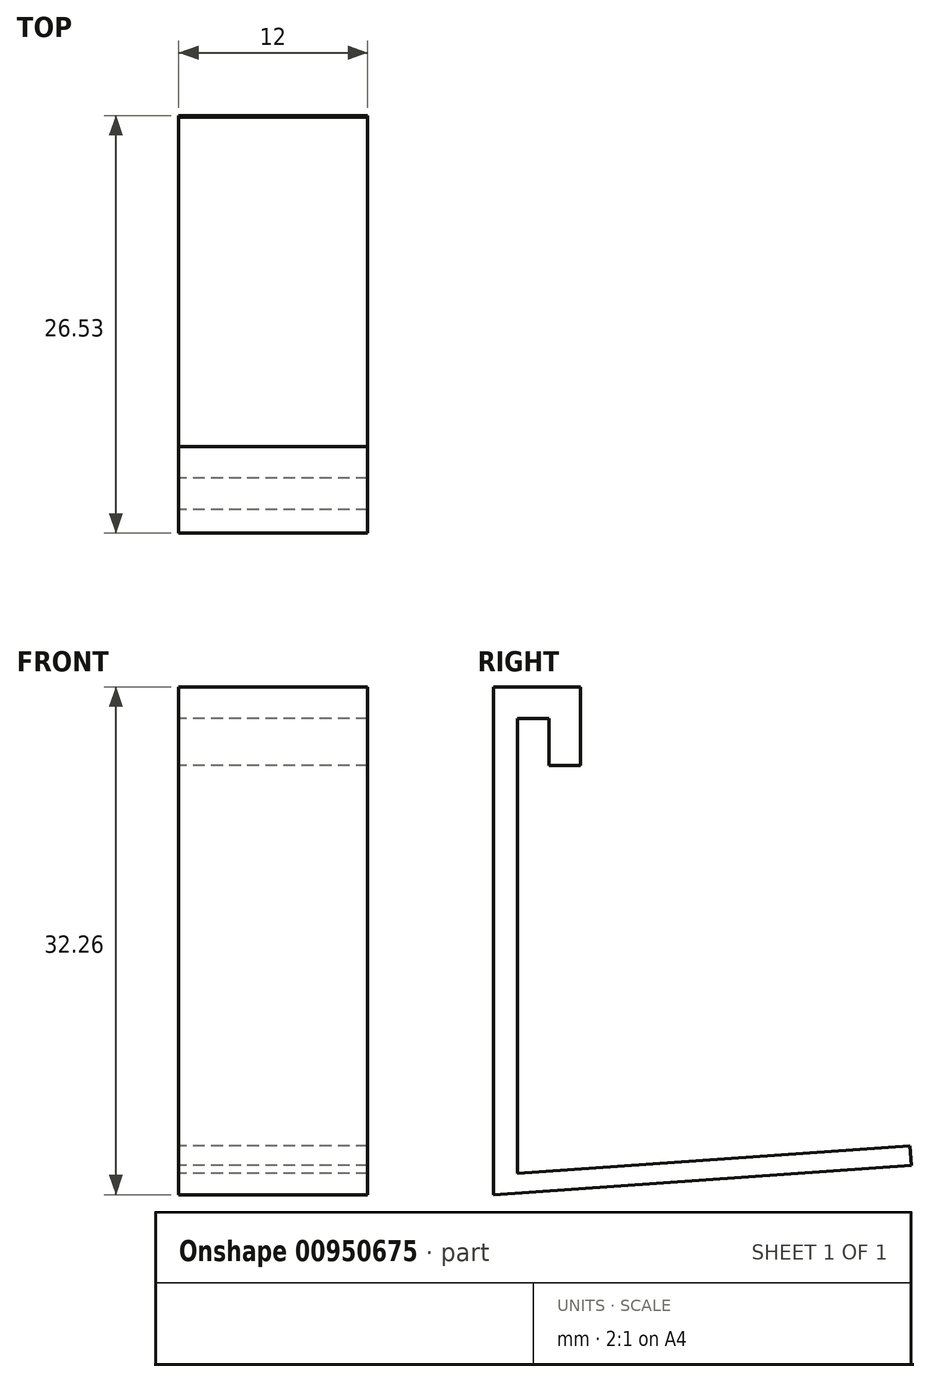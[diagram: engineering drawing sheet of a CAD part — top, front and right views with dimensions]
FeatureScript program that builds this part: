
annotation { "Feature Type Name" : "Feature", "Feature Type Description" : "" }
export const myFeature = defineFeature(function(context is Context, id is Id, definition is map)
    precondition{}
    {
        {
            var Q0;
            Q0=qCreatedBy(makeId("Front.planeOp"),FACE);
            var sketch = newSketch(context, id + "F0", { "sketchPlane" : qUnion([Q0])});
            skLineSegment(sketch, "E0.bottom", {"start": v(-42.47, 42.4) * mm, "end": v(-54.47, 42.4) * mm});
            skLineSegment(sketch, "E0.top", {"start": v(-42.47, 16.5) * mm, "end": v(-54.47, 16.5) * mm});
            skLineSegment(sketch, "E0.left", {"start": v(-42.47, 42.4) * mm, "end": v(-42.47, 16.5) * mm});
            skLineSegment(sketch, "E0.right", {"start": v(-54.47, 42.4) * mm, "end": v(-54.47, 16.5) * mm});
            skSolve(sketch);
        }
        {
            var Q0;
            Q0=makeQuery(id+"F0.imprint","IMPRINT",FACE,{"disambiguationData":[TD([[makeQuery(id+"F0.imprint","IMPRINT",EDGE,{"derivedFrom":sQuery(id+"F0.wireOp",EDGE,"E0.bottom")}),1.0]])]});
            extrude(context, id + "F1", {"entities" : qUnion([Q0]), "depth" : 1.5 * mm, "offsetDistance" : 25 * mm});
        }
        {
            var Q0;
            Q0=makeQuery(id+"F1.opExtrude","CAP_FACE",FACE,{"disambiguationData":[OSD([sQuery(id+"F0.wireOp",EDGE,"E0.bottom"),sQuery(id+"F0.wireOp",EDGE,"E0.top"),sQuery(id+"F0.wireOp",EDGE,"E0.left"),sQuery(id+"F0.wireOp",EDGE,"E0.right")])],"isStart":false});
            var sketch = newSketch(context, id + "F2", { "sketchPlane" : qUnion([Q0])});
            skLineSegment(sketch, "E1.0", {"start": v(-42.47, 16.5) * mm, "end": v(-54.47, 16.5) * mm});
            skLineSegment(sketch, "E2", {"start": v(-54.47, 16.5) * mm, "end": v(-54.47, 15.26) * mm});
            skLineSegment(sketch, "E3", {"start": v(-54.47, 15.26) * mm, "end": v(-42.47, 15.26) * mm});
            skLineSegment(sketch, "E4", {"start": v(-42.47, 15.26) * mm, "end": v(-42.47, 16.5) * mm});
            skSolve(sketch);
        }
        {
            var Q0;
            Q0=makeQuery(id+"FgG7fGiDoCPkPZg_1.boolean.opBoolean","MERGE",FACE,{"derivedFrom":[makeQuery(id+"F1.opExtrude","SWEPT_FACE",FACE,{"disambiguationData":[OSD([sQuery(id+"F0.wireOp",EDGE,"E0.right")])]}),makeQuery(id+"FgG7fGiDoCPkPZg_1.opExtrude","SWEPT_FACE",FACE,{"disambiguationData":[OSD([sQuery(id+"F2.wireOp",EDGE,"E2")])]})]});
            var sketch = newSketch(context, id + "F3", { "sketchPlane" : qUnion([Q0])});
            skLineSegment(sketch, "E5.0", {"start": v(1.5, 42.4) * mm, "end": v(1.5, 15.26) * mm});
            skLineSegment(sketch, "E5.1", {"start": v(0, 42.4) * mm, "end": v(0, 16.5) * mm});
            skLineSegment(sketch, "E5.2", {"start": v(1.5, 42.4) * mm, "end": v(0, 42.4) * mm});
            skLineSegment(sketch, "E6", {"start": v(-2, 42.4) * mm, "end": v(-4, 42.4) * mm});
            skLineSegment(sketch, "E7", {"start": v(-4, 42.4) * mm, "end": v(-4, 45.4) * mm});
            skLineSegment(sketch, "E8", {"start": v(1.5, 45.4) * mm, "end": v(1.5, 42.4) * mm});
            skLineSegment(sketch, "E9", {"start": v(-2, 42.4) * mm, "end": v(-2, 45.4) * mm});
            skLineSegment(sketch, "E10", {"start": v(-4, 45.4) * mm, "end": v(-4, 47.4) * mm});
            skLineSegment(sketch, "E11", {"start": v(1.5, 47.4) * mm, "end": v(1.5, 45.4) * mm});
            skLineSegment(sketch, "E12", {"start": v(0, 45.4) * mm, "end": v(0, 42.4) * mm});
            skLineSegment(sketch, "E13", {"start": v(0, 45.4) * mm, "end": v(-2, 45.4) * mm});
            skLineSegment(sketch, "E14", {"start": v(-4, 47.4) * mm, "end": v(1.5, 47.4) * mm});
            skSolve(sketch);
        }
        {
            var Q0;
            Q0=makeQuery(id+"F3.imprint","IMPRINT",FACE,{"disambiguationData":[TD([[makeQuery(id+"F3.imprint","IMPRINT",EDGE,{"derivedFrom":sQuery(id+"F3.wireOp",EDGE,"E5.2")}),-1.0]])]});
            var Q1;
            Q1=makeQuery(id+"FgG7fGiDoCPkPZg_1.boolean.opBoolean","MERGE",FACE,{"derivedFrom":[makeQuery(id+"F1.opExtrude","SWEPT_FACE",FACE,{"disambiguationData":[OSD([sQuery(id+"F0.wireOp",EDGE,"E0.left")])]}),makeQuery(id+"FgG7fGiDoCPkPZg_1.opExtrude","SWEPT_FACE",FACE,{"disambiguationData":[OSD([sQuery(id+"F2.wireOp",EDGE,"E4")])]})]});
            extrude(context, id + "F4", {"entities" : qUnion([Q0]), "operationType" : NewBodyOperationType.ADD, "endBound" : BoundingType.UP_TO_SURFACE, "oppositeDirection" : true, "depth" : 25 * mm, "endBoundEntityFace" : qUnion([Q1]), "offsetDistance" : 25 * mm});
        }
        {
            var Q0;
            Q0=makeQuery(id+"F4.boolean.opBoolean","MERGE",FACE,{"derivedFrom":[makeQuery(id+"F1.opExtrude","SWEPT_FACE",FACE,{"disambiguationData":[OSD([sQuery(id+"F0.wireOp",EDGE,"E0.right")])]}),makeQuery(id+"F4.opExtrude","CAP_FACE",FACE,{"disambiguationData":[OSD([sQuery(id+"F3.wireOp",EDGE,"E5.2"),sQuery(id+"F3.wireOp",EDGE,"E6"),sQuery(id+"F3.wireOp",EDGE,"E7"),sQuery(id+"F3.wireOp",EDGE,"E8"),sQuery(id+"F3.wireOp",EDGE,"E9"),sQuery(id+"F3.wireOp",EDGE,"E10"),sQuery(id+"F3.wireOp",EDGE,"E11"),sQuery(id+"F3.wireOp",EDGE,"E12"),sQuery(id+"F3.wireOp",EDGE,"E13"),sQuery(id+"F3.wireOp",EDGE,"E14")])],"isStart":true})]});
            var sketch = newSketch(context, id + "F5", { "sketchPlane" : qUnion([Q0])});
            skLineSegment(sketch, "E15", {"start": v(0, 16.5) * mm, "end": v(-24.94, 18.25) * mm});
            skLineSegment(sketch, "E16", {"start": v(-24.94, 18.25) * mm, "end": v(-25.03, 17) * mm});
            skLineSegment(sketch, "E17", {"start": v(-25.03, 17) * mm, "end": v(1.5, 15.15) * mm});
            skLineSegment(sketch, "E18", {"start": v(1.5, 15.15) * mm, "end": v(1.5, 16.5) * mm});
            skSolve(sketch);
        }
        {
            var Q0;
            Q0=makeQuery(id+"F5.imprint","IMPRINT",FACE,{"disambiguationData":[TD([[makeQuery(id+"F5.imprint","IMPRINT",EDGE,{"derivedFrom":sQuery(id+"F5.wireOp",EDGE,"E15")}),1.0]])]});
            var Q1;
            Q1=makeQuery(id+"F4.boolean.opBoolean","MERGE",FACE,{"derivedFrom":[makeQuery(id+"F1.opExtrude","SWEPT_FACE",FACE,{"disambiguationData":[OSD([sQuery(id+"F0.wireOp",EDGE,"E0.left")])]}),makeQuery(id+"F4.opExtrude","CAP_FACE",FACE,{"disambiguationData":[OSD([sQuery(id+"F3.wireOp",EDGE,"E5.2"),sQuery(id+"F3.wireOp",EDGE,"E6"),sQuery(id+"F3.wireOp",EDGE,"E7"),sQuery(id+"F3.wireOp",EDGE,"E8"),sQuery(id+"F3.wireOp",EDGE,"E9"),sQuery(id+"F3.wireOp",EDGE,"E10"),sQuery(id+"F3.wireOp",EDGE,"E11"),sQuery(id+"F3.wireOp",EDGE,"E12"),sQuery(id+"F3.wireOp",EDGE,"E13"),sQuery(id+"F3.wireOp",EDGE,"E14")])],"isStart":false})]});
            extrude(context, id + "F6", {"entities" : qUnion([Q0]), "operationType" : NewBodyOperationType.ADD, "endBound" : BoundingType.UP_TO_SURFACE, "oppositeDirection" : true, "depth" : 25 * mm, "endBoundEntityFace" : qUnion([Q1]), "offsetDistance" : 25 * mm});
        }
    });
